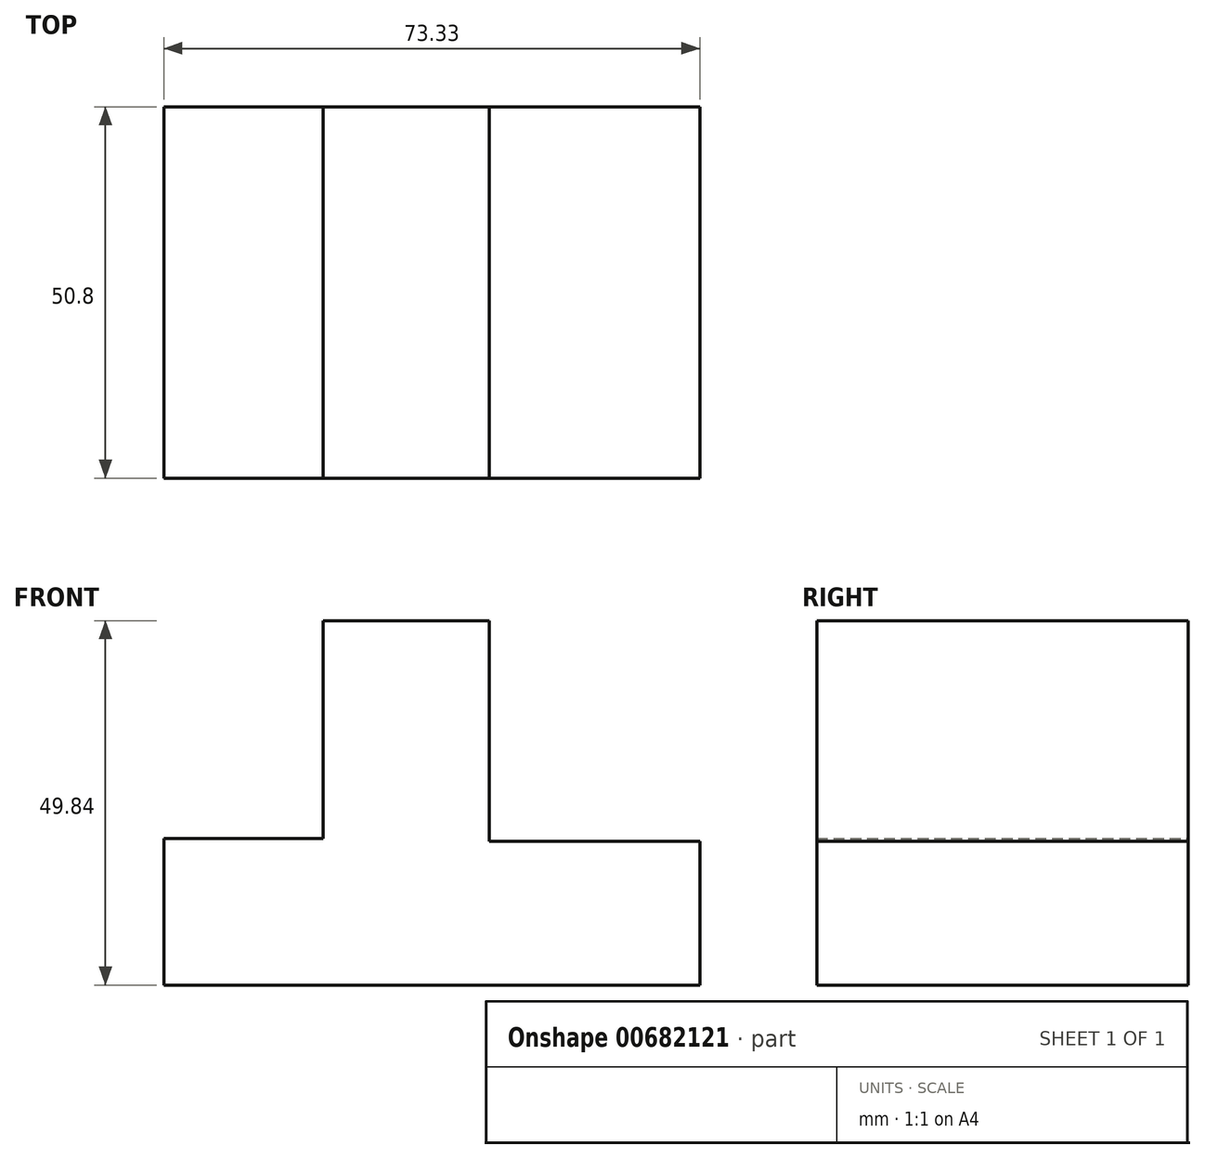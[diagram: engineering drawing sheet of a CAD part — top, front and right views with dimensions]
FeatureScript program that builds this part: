
annotation { "Feature Type Name" : "Feature", "Feature Type Description" : "" }
export const myFeature = defineFeature(function(context is Context, id is Id, definition is map)
    precondition{}
    {
        {
            var Q0;
            Q0=qCreatedBy(makeId("Front.planeOp"),FACE);
            var sketch = newSketch(context, id + "F0", { "sketchPlane" : qUnion([Q0])});
            skLineSegment(sketch, "E0", {"start": v(-46.88, 13.84) * mm, "end": v(-25.11, 13.84) * mm});
            skLineSegment(sketch, "E1", {"start": v(-25.11, 13.84) * mm, "end": v(-25.11, 43.63) * mm});
            skLineSegment(sketch, "E2", {"start": v(-25.11, 43.63) * mm, "end": v(-2.39, 43.63) * mm});
            skLineSegment(sketch, "E3", {"start": v(-2.39, 43.63) * mm, "end": v(-2.39, 13.46) * mm});
            skLineSegment(sketch, "E4", {"start": v(-2.39, 13.46) * mm, "end": v(26.45, 13.46) * mm});
            skLineSegment(sketch, "E5", {"start": v(26.45, 13.46) * mm, "end": v(26.45, -6.2) * mm});
            skLineSegment(sketch, "E6", {"start": v(26.45, -6.2) * mm, "end": v(-46.88, -6.2) * mm});
            skLineSegment(sketch, "E7", {"start": v(-46.88, -6.2) * mm, "end": v(-46.88, 13.84) * mm});
            skPoint(sketch, "E8.orphan", {"position": v(-48.4, 13.84) * mm});
            skSolve(sketch);
        }
        {
            var Q0;
            Q0 = qSketchRegion(id + "F0", true);
            extrude(context, id + "F1", {"entities" : qUnion([Q0]), "depth" : 50.8 * mm, "offsetDistance" : 25.4 * mm});
        }
    });
